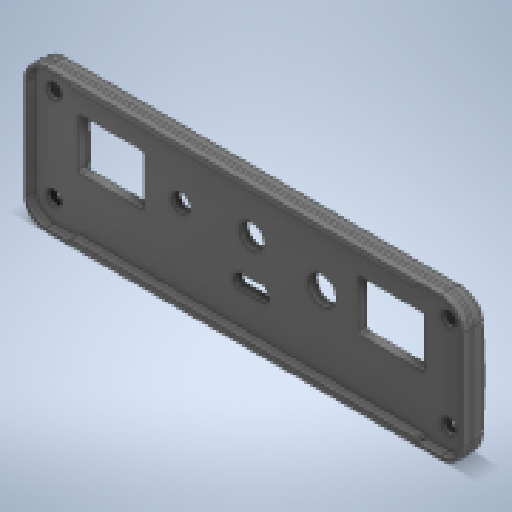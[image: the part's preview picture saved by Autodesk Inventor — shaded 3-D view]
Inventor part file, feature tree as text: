
AUTODESK INVENTOR PART (.ipt)
format: ipt  version: 2023.2 (Build 272271000, 271)  size: 510,976 bytes
history: native  units: mm
features: reference x30, other x5, extrude x1, fillet x1, sketch x1
ambient origin geometry x8: Origin, YZ Plane, XZ Plane, XY Plane, X Axis, Y Axis, Z Axis, Center Point
bodies: Solid2 (feature_tree), Solid1 (feature_tree)
feature tree (38):
  extrude  "Extrusion1"  Depth=10.0mm
  fillet  "Fillet1"  Radius=0.5mm
  sketch  "Sketch1"  dims[d1=0.5mm d2=0.5mm d3=0.5mm d4=0.5mm d5=0.5mm d9=0.5mm d10=0.5mm d11=0.5mm d12=0.5mm d13=0.5mm d14=0.5mm d15=10.0mm d16=0.0mm d19=0.2mm]
  reference  "Reference1"
  reference  "Reference2"
  reference  "Reference3"
  reference  "Reference4"
  reference  "Reference5"
  reference  "Reference6"
  reference  "Reference7"
  reference  "Reference8"
  reference  "Reference9"
  reference  "Reference10"
  reference  "Reference11"
  reference  "Reference12"
  reference  "Reference13"
  reference  "Reference14"
  reference  "Reference15"
  reference  "Reference16"
  reference  "Reference17"
  reference  "Reference18"
  reference  "Reference19"
  reference  "Reference20"
  reference  "Reference21"
  reference  "Reference22"
  reference  "Reference23"
  reference  "Reference24"
  reference  "Reference25"
  reference  "Reference26"
  reference  "Reference27"
  reference  "Reference28"
  reference  "Reference29"
  reference  "Reference30"
  parser-record x1  (decoder bookkeeping rows leaked as tree rows — omitted from the tree; the rows remain in map.json)
  other  "ND.NeuroLink._Main.iam"
  other  "BaseBoard:1"
  other  "Raspberry Pi Pico-R3:1"
  other  "MicroUSB Port, Raspberry Pi Pico-R3:1"
note: 1 file-system path scrubbed to <path> (originals preserved in map.json)
